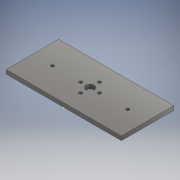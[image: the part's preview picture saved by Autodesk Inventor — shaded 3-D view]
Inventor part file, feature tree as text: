
AUTODESK INVENTOR PART (.ipt)
format: ipt  version: 2018 (Build 220112000, 112)  size: 119,808 bytes
history: native  units: mm
features: sketch x2, other x1, extrude x1
ambient origin geometry x8: Origin, YZ Plane, XZ Plane, XY Plane, X Axis, Y Axis, Z Axis, Center Point
bodies: Body1 (feature_tree)
feature tree (4):
  other  "Sólido1"
  extrude  "Extrusión1"  Depth=25.0mm
  sketch  "Boceto2"  dims[d2=4.0mm d4=1.5mm d8=1.5mm d9=1.5mm d10=1.5mm d15=1.5mm d16=1.5mm d17=2.0mm d18=0.0mm]
  sketch  "Boceto1"  dims[d0=55.0mm d1=25.0mm]
